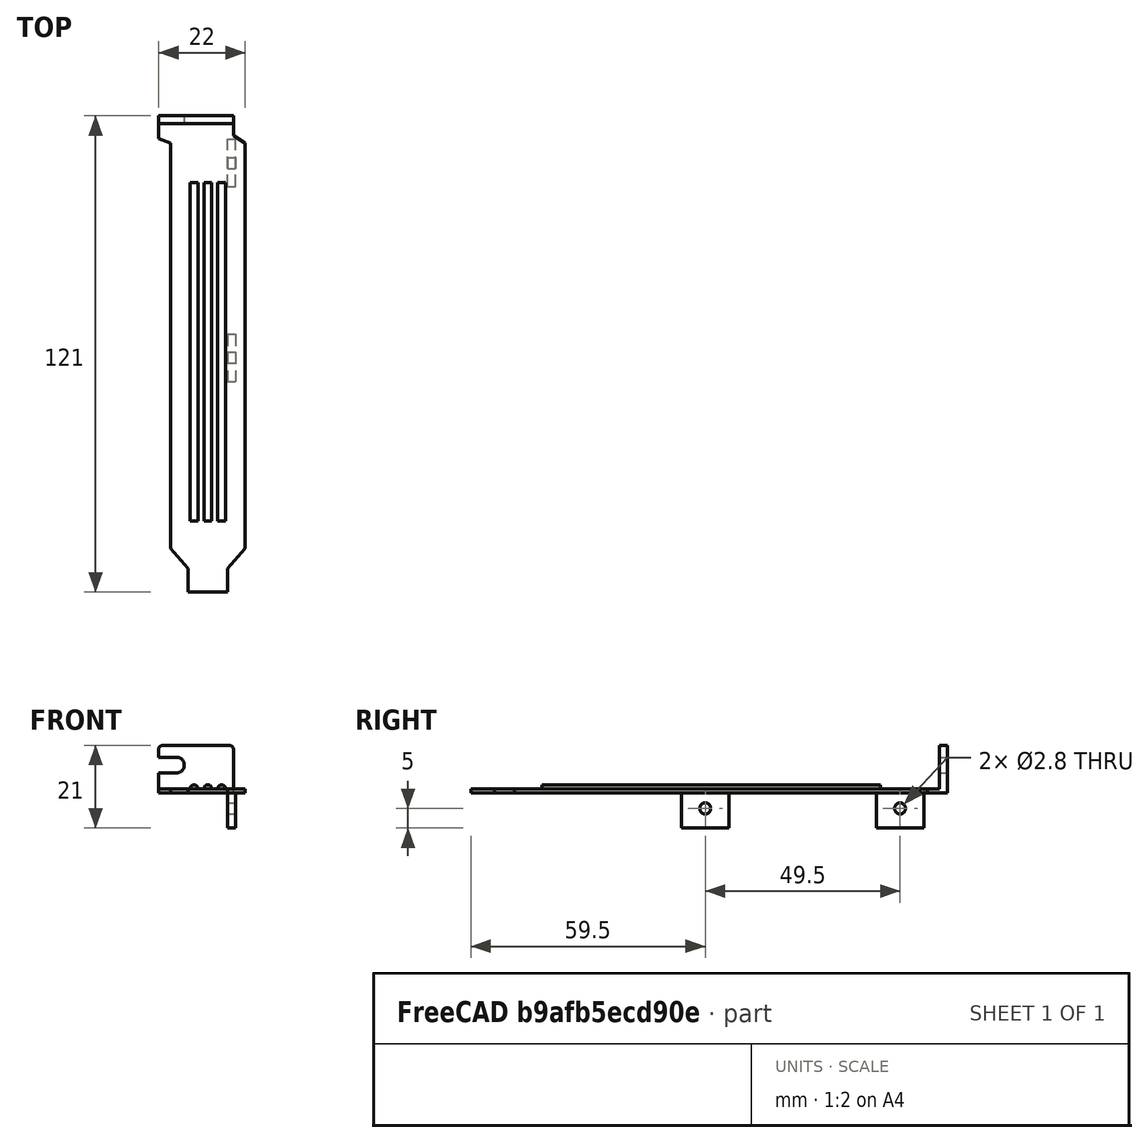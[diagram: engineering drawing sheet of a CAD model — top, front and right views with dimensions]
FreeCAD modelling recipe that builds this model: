
FCSTD DOCUMENT  (FreeCAD 0.18.4R)
Label: A26x0 Slot Cover
License: All rights reserved
LicenseURL: http://en.wikipedia.org/wiki/All_rights_reserved
objects: PartDesign::AdditiveBox×5, PartDesign::SubtractiveWedge×4, PartDesign::SubtractiveCylinder×3, PartDesign::AdditiveCylinder×3, PartDesign::SubtractiveBox×1, PartDesign::Fillet×1, PartDesign::Body×1
note: 34 computed .brp shape members not serialized (recipe doc carries the construction recipe); baked Part::Feature solids carry a one-line shape summary decoded from their .brp

FEATURE [PartDesign::AdditiveBox] Box
  AttacherType = Attacher::AttachEngine3D
  AttachmentOffset = pos=(-9.5,-60,0) rot=(0,0,1;0rad)
  Height = 1
  Length = 19
  MapMode = 5
  Placement = pos=(-9.5,-60,0) rot=(0,0,1;0rad)
  Refine = true
  Support = -> [XY_Plane]
  Width = 114
FEATURE [PartDesign::SubtractiveWedge] Wedge
  AttacherType = Attacher::AttachEngine3D
  AttachmentOffset = pos=(5,-54,-1) rot=(0,0,-1;1.5708rad)
  BaseFeature = -> Box
  MapMode = 5
  Placement = pos=(5,-54,-1) rot=(0,0,-1;1.5708rad)
  Refine = true
  Support = -> [XY_Plane]
  X2max = 7
  X2min = -5
  Xmax = 7
  Xmin = 0
  Ymax = 4.5
  Ymin = 0
  Z2max = 5
  Z2min = 0
  Zmax = 5
  Zmin = 0
FEATURE [PartDesign::SubtractiveWedge] Wedge001
  AttacherType = Attacher::AttachEngine3D
  AttachmentOffset = pos=(5,-54,-1) rot=(0,0,-1;1.5708rad)
  BaseFeature = -> Wedge
  MapMode = 2
  Placement = pos=(-5,-54,1) rot=(-0.707107,0.707107,0;3.14159rad)
  Refine = true
  Support = -> [XY_Plane]
  X2max = 7
  X2min = -5
  Xmax = 7
  Xmin = 0
  Ymax = 4.5
  Ymin = 0
  Z2max = 5
  Z2min = 0
  Zmax = 5
  Zmin = 0
FEATURE [PartDesign::AdditiveBox] Box001
  AttacherType = Attacher::AttachEngine3D
  AttachmentOffset = pos=(-12.5,54,0) rot=(0,0,1;0rad)
  BaseFeature = -> Wedge001
  Height = 1
  Length = 22
  MapMode = 5
  Placement = pos=(-12.5,54,0) rot=(0,0,1;0rad)
  Refine = true
  Support = -> [XY_Plane]
  Width = 7
FEATURE [PartDesign::SubtractiveWedge] Wedge002
  AttacherType = Attacher::AttachEngine3D
  AttachmentOffset = pos=(6.5,60,0) rot=(0,0,-1;1.5708rad)
  BaseFeature = -> Box001
  MapMode = 5
  Placement = pos=(6.5,60,0) rot=(0,0,-1;1.5708rad)
  Refine = true
  Support = -> [XY_Plane]
  X2max = 6
  X2min = -1
  Xmax = 4
  Xmin = -1
  Ymax = 3
  Ymin = 0
  Z2max = 4
  Z2min = 0
  Zmax = 5
  Zmin = 0
FEATURE [PartDesign::SubtractiveWedge] Wedge003
  AttacherType = Attacher::AttachEngine3D
  AttachmentOffset = pos=(-19.5,54,0) rot=(0,0,1;0rad)
  BaseFeature = -> Wedge002
  MapMode = 5
  Placement = pos=(-19.5,54,0) rot=(0,0,1;0rad)
  Refine = true
  Support = -> [XY_Plane]
  X2max = 5
  X2min = 0
  Xmax = 10
  Xmin = 0
  Ymax = 2
  Ymin = 0
  Z2max = 1
  Z2min = 0
  Zmax = 1
  Zmin = 0
FEATURE [PartDesign::AdditiveBox] Box002
  AttacherType = Attacher::AttachEngine3D
  AttachmentOffset = pos=(-12.5,59,0) rot=(0,0,1;0rad)
  BaseFeature = -> Wedge003
  Height = 12
  Length = 19
  MapMode = 5
  Placement = pos=(-12.5,59,0) rot=(0,0,1;0rad)
  Refine = true
  Support = -> [XY_Plane]
  Width = 2
FEATURE [PartDesign::SubtractiveCylinder] Cylinder
  Angle = 360
  AttacherType = Attacher::AttachEngine3D
  AttachmentOffset = pos=(-8,7,-61) rot=(0,0,1;0rad)
  BaseFeature = -> Box002
  Height = 2
  MapMode = 3
  Placement = pos=(-8,61,7) rot=(1,0,0;1.5708rad)
  Radius = 2
  Refine = true
  Support = -> [XY_Plane]
FEATURE [PartDesign::SubtractiveBox] Box003
  AttacherType = Attacher::AttachEngine3D
  AttachmentOffset = pos=(-13,59,5) rot=(0,0,1;0rad)
  BaseFeature = -> Cylinder
  Height = 4
  Length = 5
  MapMode = 5
  Placement = pos=(-13,59,5) rot=(0,0,1;0rad)
  Refine = true
  Support = -> [XY_Plane]
  Width = 2
FEATURE [PartDesign::Fillet] Fillet
  Base = -> Box003 [Edge46,Edge54]
  BaseFeature = -> Box003
  Placement = pos=(-13,59,5) rot=(0,0,1;0rad)
  Radius = 1
FEATURE [PartDesign::AdditiveCylinder] Cylinder001
  Angle = 180
  AttacherType = Attacher::AttachEngine3D
  AttachmentOffset = pos=(0,1,-44) rot=(0,0,1;0rad)
  BaseFeature = -> Fillet
  Height = 86
  MapMode = 5
  Placement = pos=(0,44,1) rot=(1,0,0;1.5708rad)
  Radius = 1
  Refine = true
  Support = -> [XZ_Plane]
FEATURE [PartDesign::AdditiveCylinder] Cylinder002
  Angle = 180
  AttacherType = Attacher::AttachEngine3D
  AttachmentOffset = pos=(3.5,1,-44) rot=(0,0,1;0rad)
  BaseFeature = -> Cylinder001
  Height = 86
  MapMode = 5
  Placement = pos=(3.5,44,1) rot=(1,0,0;1.5708rad)
  Radius = 1
  Refine = true
  Support = -> [XZ_Plane]
FEATURE [PartDesign::AdditiveCylinder] Cylinder003
  Angle = 180
  AttacherType = Attacher::AttachEngine3D
  AttachmentOffset = pos=(-3.5,1,-44) rot=(0,0,1;0rad)
  BaseFeature = -> Cylinder002
  Height = 86
  MapMode = 5
  Placement = pos=(-3.5,44,1) rot=(1,0,0;1.5708rad)
  Radius = 1
  Refine = true
  Support = -> [XZ_Plane]
FEATURE [PartDesign::AdditiveBox] Box004  label="UpperBrace"
  AttacherType = Attacher::AttachEngine3D
  AttachmentOffset = pos=(5,43,-9) rot=(0,0,1;0rad)
  BaseFeature = -> Cylinder003
  Height = 9
  Length = 2
  MapMode = 2
  Placement = pos=(5,43,-9) rot=(0,0,1;0rad)
  Refine = true
  Support = -> [XY_Plane]
  Width = 12
FEATURE [PartDesign::SubtractiveCylinder] Cylinder004  label="UpperBraceHole"
  Angle = 360
  AttacherType = Attacher::AttachEngine3D
  AttachmentOffset = pos=(49,-4,5) rot=(0,0,1;0rad)
  BaseFeature = -> Box004
  Height = 2
  MapMode = 2
  Placement = pos=(5,49,-4) rot=(0.57735,0.57735,0.57735;2.0944rad)
  Radius = 1.4
  Refine = true
  Support = -> [YZ_Plane]
FEATURE [PartDesign::AdditiveBox] Box005  label="LowerBrace"
  AttacherType = Attacher::AttachEngine3D
  AttachmentOffset = pos=(-6.5,-9,5) rot=(0,0,1;0rad)
  BaseFeature = -> Cylinder004
  Height = 2
  Length = 12
  MapMode = 2
  Placement = pos=(5,-6.5,-9) rot=(0.57735,0.57735,0.57735;2.0944rad)
  Refine = true
  Support = -> [YZ_Plane]
  Width = 10
FEATURE [PartDesign::SubtractiveCylinder] Cylinder005  label="LowerBraceHole"
  Angle = 360
  AttacherType = Attacher::AttachEngine3D
  AttachmentOffset = pos=(-0.5,-4,5) rot=(0,0,1;0rad)
  BaseFeature = -> Box005
  Height = 2
  MapMode = 2
  Placement = pos=(5,-0.5,-4) rot=(0.57735,0.57735,0.57735;2.0944rad)
  Radius = 1.4
  Refine = true
  Support = -> [YZ_Plane]
FEATURE [PartDesign::Body] Body  label="Amiga-EATX-Slot-Bracket"
  Group = -> [Box,Wedge,Wedge001,Box001,Wedge002,Wedge003,Box002,Cylinder,Box003,Fillet,Cylinder001,Cylinder002,Cylinder003,Box004,Cylinder004,Box005,Cylinder005]
  Origin = -> Origin
  Tip = -> Cylinder005
